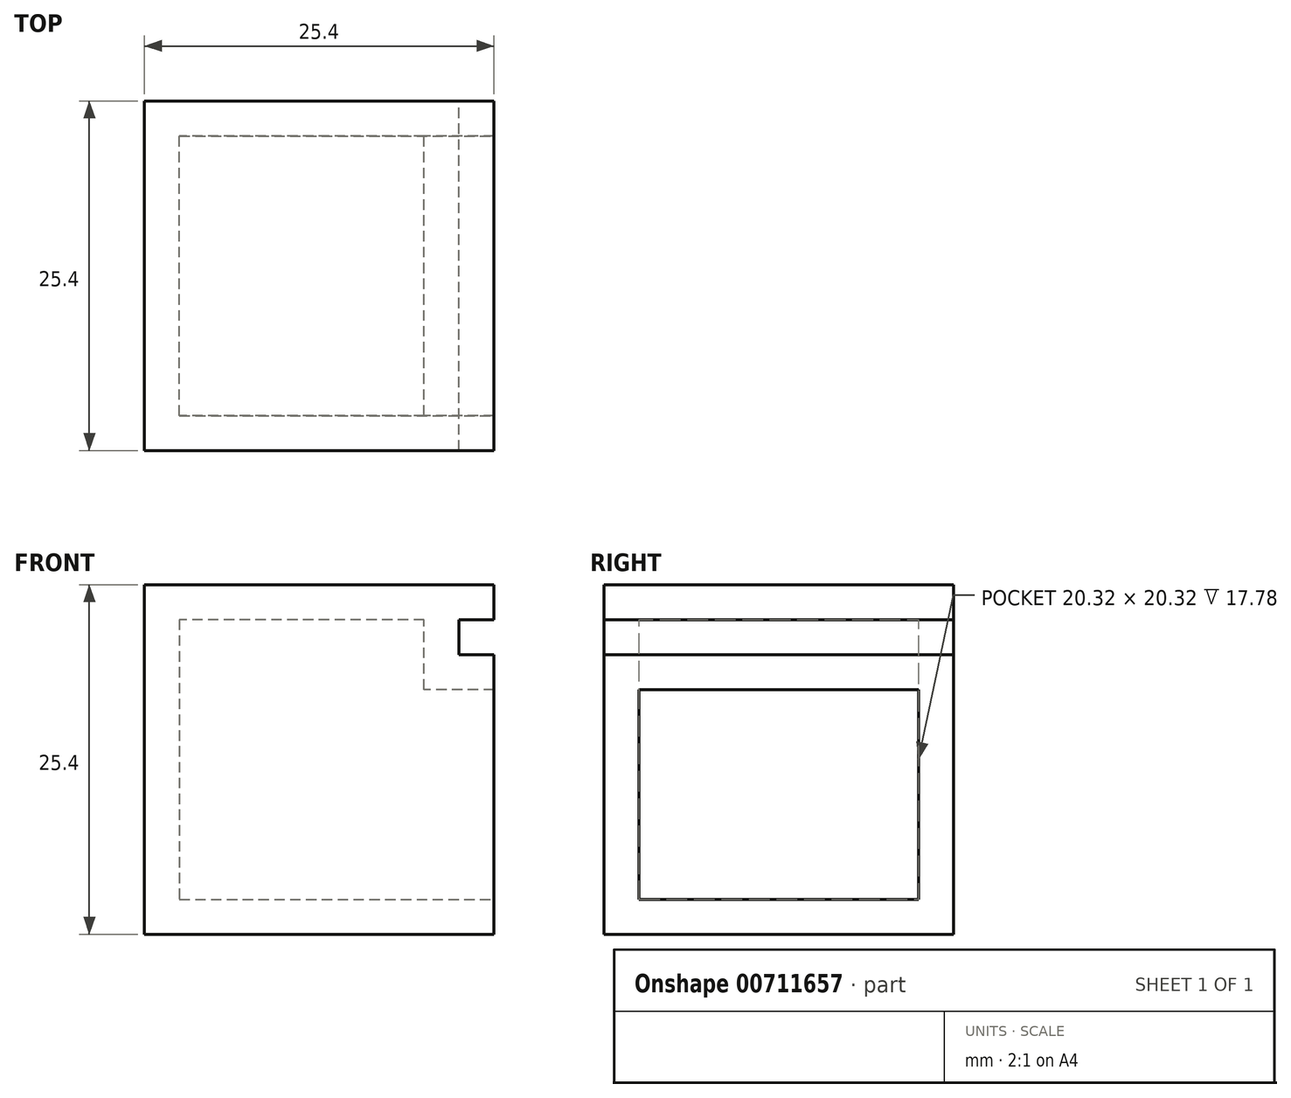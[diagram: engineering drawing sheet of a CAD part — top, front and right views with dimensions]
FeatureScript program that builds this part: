
annotation { "Feature Type Name" : "Feature", "Feature Type Description" : "" }
export const myFeature = defineFeature(function(context is Context, id is Id, definition is map)
    precondition{}
    {
        {
            var Q0;
            Q0=qCreatedBy(makeId("Front.planeOp"),FACE);
            var sketch = newSketch(context, id + "F0", { "sketchPlane" : qUnion([Q0])});
            skLineSegment(sketch, "E0", {"start": v(0, 0) * mm, "end": v(25.4, 0) * mm});
            skLineSegment(sketch, "E1", {"start": v(25.4, 0) * mm, "end": v(25.4, 20.32) * mm});
            skLineSegment(sketch, "E2", {"start": v(25.4, 20.32) * mm, "end": v(22.86, 20.32) * mm});
            skLineSegment(sketch, "E3", {"start": v(22.86, 20.32) * mm, "end": v(22.86, 22.86) * mm});
            skLineSegment(sketch, "E4", {"start": v(22.86, 22.86) * mm, "end": v(25.4, 22.86) * mm});
            skLineSegment(sketch, "E5", {"start": v(25.4, 22.86) * mm, "end": v(25.4, 25.4) * mm});
            skLineSegment(sketch, "E6", {"start": v(25.4, 25.4) * mm, "end": v(0, 25.4) * mm});
            skLineSegment(sketch, "E7", {"start": v(0, 25.4) * mm, "end": v(0, 0) * mm});
            skSolve(sketch);
        }
        {
            var Q0;
            Q0=makeQuery(id+"F0.imprint","IMPRINT",FACE,{"disambiguationData":[TD([[makeQuery(id+"F0.imprint","IMPRINT",EDGE,{"derivedFrom":sQuery(id+"F0.wireOp",EDGE,"E0")}),1.0]])]});
            extrude(context, id + "F1", {"entities" : qUnion([Q0]), "depth" : 25.4 * mm, "offsetDistance" : 25.4 * mm});
        }
        {
            var Q0;
            Q0=makeQuery(id+"F1.opExtrude","SWEPT_FACE",FACE,{"disambiguationData":[OSD([sQuery(id+"F0.wireOp",EDGE,"E1")])]});
            shell(context, id + "F2", {"entities" : qUnion([Q0]), "thickness" : 2.54 * mm});
        }
    });
